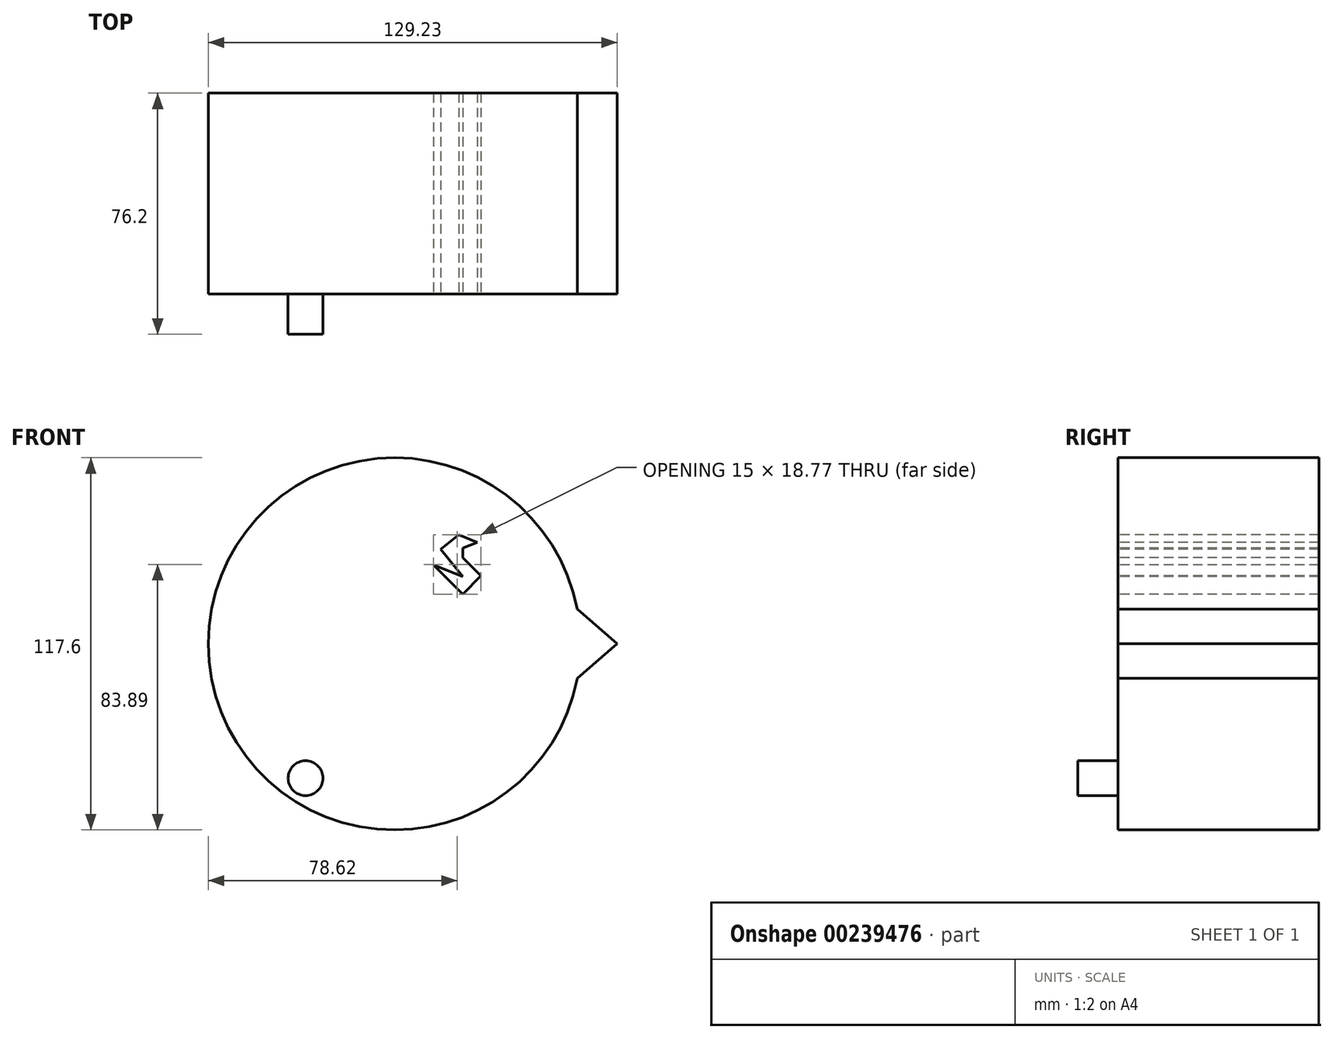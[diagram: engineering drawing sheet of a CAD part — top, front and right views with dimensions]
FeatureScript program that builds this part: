
annotation { "Feature Type Name" : "Feature", "Feature Type Description" : "" }
export const myFeature = defineFeature(function(context is Context, id is Id, definition is map)
    precondition{}
    {
        {
            var Q0;
            Q0=qCreatedBy(makeId("Front.planeOp"),FACE);
            var sketch = newSketch(context, id + "F0", { "sketchPlane" : qUnion([Q0])});
            skCircle(sketch, "E0", {"center": v(0, 0) * mm, "radius": 58.8 * mm});
            skSolve(sketch);
        }
        {
            var Q0;
            Q0=makeQuery(id+"F0.imprint","IMPRINT",FACE,{"disambiguationData":[TD([[makeQuery(id+"F0.imprint","IMPRINT",EDGE,{"derivedFrom":sQuery(id+"F0.wireOp",EDGE,"E0")}),1.0]])]});
            extrude(context, id + "F1", {"entities" : qUnion([Q0]), "endBound" : BoundingType.SYMMETRIC, "depth" : 63.5 * mm});
        }
        {
            var Q0;
            Q0=makeQuery(id+"F1.opExtrude","CAP_FACE",FACE,{"disambiguationData":[OSD([sQuery(id+"F0.wireOp",EDGE,"E0")])],"isStart":false});
            var sketch = newSketch(context, id + "F2", { "sketchPlane" : qUnion([Q0])});
            skCircle(sketch, "E1", {"center": v(-28.08, -42.43) * mm, "radius": 5.5 * mm});
            skSolve(sketch);
        }
        {
            var Q0;
            Q0=makeQuery(id+"F2.imprint","IMPRINT",FACE,{"disambiguationData":[TD([[makeQuery(id+"F2.imprint","IMPRINT",EDGE,{"derivedFrom":sQuery(id+"F2.wireOp",EDGE,"E1")}),1.0]])]});
            extrude(context, id + "F3", {"entities" : qUnion([Q0]), "operationType" : NewBodyOperationType.ADD, "depth" : 12.7 * mm});
        }
        {
            var Q0;
            Q0=makeQuery(id+"F1.opExtrude","CAP_FACE",FACE,{"disambiguationData":[OSD([sQuery(id+"F0.wireOp",EDGE,"E0")])],"isStart":false});
            var sketch = newSketch(context, id + "F4", { "sketchPlane" : qUnion([Q0])});
            skLineSegment(sketch, "E2", {"start": v(57.78, 10.93) * mm, "end": v(70.43, 0) * mm});
            skLineSegment(sketch, "E3", {"start": v(70.43, 0) * mm, "end": v(57.78, -10.93) * mm});
            skArc(sketch, "E4.0", {"start": v(57.78, -10.93) * mm, "mid": v(58.8, 0) * mm, "end": v(57.78, 10.93) * mm});
            skSolve(sketch);
        }
        {
            var Q0;
            Q0 = qSketchRegion(id + "F4", true);
            extrude(context, id + "F5", {"entities" : qUnion([Q0]), "operationType" : NewBodyOperationType.ADD, "oppositeDirection" : true, "depth" : 63.5 * mm});
        }
        {
            var Q0;
            {var subQ0=sQuery(id+"F4.wireOp",EDGE,"E4.0");var subQ1=sQuery(id+"F4.wireOp",EDGE,"E3");var subQ2=sQuery(id+"F4.wireOp",EDGE,"E2");Q0=makeQuery(id+"FHikPiwag3CsCLX_1.16.F5.boolean.opBoolean","MERGE",FACE,{"derivedFrom":[makeQuery(id+"FHikPiwag3CsCLX_1.15.F5.boolean.opBoolean","MERGE",FACE,{"derivedFrom":[makeQuery(id+"FHikPiwag3CsCLX_1.14.F5.boolean.opBoolean","MERGE",FACE,{"derivedFrom":[makeQuery(id+"FHikPiwag3CsCLX_1.13.F5.boolean.opBoolean","MERGE",FACE,{"derivedFrom":[makeQuery(id+"FHikPiwag3CsCLX_1.12.F5.boolean.opBoolean","MERGE",FACE,{"derivedFrom":[makeQuery(id+"FHikPiwag3CsCLX_1.11.F5.boolean.opBoolean","MERGE",FACE,{"derivedFrom":[makeQuery(id+"FHikPiwag3CsCLX_1.10.F5.boolean.opBoolean","MERGE",FACE,{"derivedFrom":[makeQuery(id+"FHikPiwag3CsCLX_1.9.F5.boolean.opBoolean","MERGE",FACE,{"derivedFrom":[makeQuery(id+"FHikPiwag3CsCLX_1.8.F5.boolean.opBoolean","MERGE",FACE,{"derivedFrom":[makeQuery(id+"FHikPiwag3CsCLX_1.7.F5.boolean.opBoolean","MERGE",FACE,{"derivedFrom":[makeQuery(id+"FHikPiwag3CsCLX_1.6.F5.boolean.opBoolean","MERGE",FACE,{"derivedFrom":[makeQuery(id+"FHikPiwag3CsCLX_1.5.F5.boolean.opBoolean","MERGE",FACE,{"derivedFrom":[makeQuery(id+"FHikPiwag3CsCLX_1.4.F5.boolean.opBoolean","MERGE",FACE,{"derivedFrom":[makeQuery(id+"FHikPiwag3CsCLX_1.3.F5.boolean.opBoolean","MERGE",FACE,{"derivedFrom":[makeQuery(id+"FHikPiwag3CsCLX_1.2.F5.boolean.opBoolean","MERGE",FACE,{"derivedFrom":[makeQuery(id+"FHikPiwag3CsCLX_1.1.F5.boolean.opBoolean","MERGE",FACE,{"derivedFrom":[makeQuery(id+"F5.boolean.opBoolean","MERGE",FACE,{"derivedFrom":[makeQuery(id+"F1.opExtrude","CAP_FACE",FACE,{"disambiguationData":[OSD([sQuery(id+"F0.wireOp",EDGE,"E0")])],"isStart":false}),makeQuery(id+"F5.opExtrude","CAP_FACE",FACE,{"disambiguationData":[OSD([subQ2,subQ1,subQ0])],"isStart":true})]}),makeQuery(id+"FHikPiwag3CsCLX_1.1.F5.opExtrude","CAP_FACE",FACE,{"disambiguationData":[OSD([subQ2,subQ1,subQ0])],"isStart":true})]}),makeQuery(id+"FHikPiwag3CsCLX_1.2.F5.opExtrude","CAP_FACE",FACE,{"disambiguationData":[OSD([subQ2,subQ1,subQ0])],"isStart":true})]}),makeQuery(id+"FHikPiwag3CsCLX_1.3.F5.opExtrude","CAP_FACE",FACE,{"disambiguationData":[OSD([subQ2,subQ1,subQ0])],"isStart":true})]}),makeQuery(id+"FHikPiwag3CsCLX_1.4.F5.opExtrude","CAP_FACE",FACE,{"disambiguationData":[OSD([subQ2,subQ1,subQ0])],"isStart":true})]}),makeQuery(id+"FHikPiwag3CsCLX_1.5.F5.opExtrude","CAP_FACE",FACE,{"disambiguationData":[OSD([subQ2,subQ1,subQ0])],"isStart":true})]}),makeQuery(id+"FHikPiwag3CsCLX_1.6.F5.opExtrude","CAP_FACE",FACE,{"disambiguationData":[OSD([subQ2,subQ1,subQ0])],"isStart":true})]}),makeQuery(id+"FHikPiwag3CsCLX_1.7.F5.opExtrude","CAP_FACE",FACE,{"disambiguationData":[OSD([subQ2,subQ1,subQ0])],"isStart":true})]}),makeQuery(id+"FHikPiwag3CsCLX_1.8.F5.opExtrude","CAP_FACE",FACE,{"disambiguationData":[OSD([subQ2,subQ1,subQ0])],"isStart":true})]}),makeQuery(id+"FHikPiwag3CsCLX_1.9.F5.opExtrude","CAP_FACE",FACE,{"disambiguationData":[OSD([subQ2,subQ1,subQ0])],"isStart":true})]}),makeQuery(id+"FHikPiwag3CsCLX_1.10.F5.opExtrude","CAP_FACE",FACE,{"disambiguationData":[OSD([subQ2,subQ1,subQ0])],"isStart":true})]}),makeQuery(id+"FHikPiwag3CsCLX_1.11.F5.opExtrude","CAP_FACE",FACE,{"disambiguationData":[OSD([subQ2,subQ1,subQ0])],"isStart":true})]}),makeQuery(id+"FHikPiwag3CsCLX_1.12.F5.opExtrude","CAP_FACE",FACE,{"disambiguationData":[OSD([subQ2,subQ1,subQ0])],"isStart":true})]}),makeQuery(id+"FHikPiwag3CsCLX_1.13.F5.opExtrude","CAP_FACE",FACE,{"disambiguationData":[OSD([subQ2,subQ1,subQ0])],"isStart":true})]}),makeQuery(id+"FHikPiwag3CsCLX_1.14.F5.opExtrude","CAP_FACE",FACE,{"disambiguationData":[OSD([subQ2,subQ1,subQ0])],"isStart":true})]}),makeQuery(id+"FHikPiwag3CsCLX_1.15.F5.opExtrude","CAP_FACE",FACE,{"disambiguationData":[OSD([subQ2,subQ1,subQ0])],"isStart":true})]}),makeQuery(id+"FHikPiwag3CsCLX_1.16.F5.opExtrude","CAP_FACE",FACE,{"disambiguationData":[OSD([subQ2,subQ1,subQ0])],"isStart":true})]});}
            var sketch = newSketch(context, id + "F6", { "sketchPlane" : qUnion([Q0])});
            skLineSegment(sketch, "E5", {"start": v(21.55, 27.24) * mm, "end": v(27.32, 21.47) * mm});
            skLineSegment(sketch, "E6", {"start": v(27.32, 21.47) * mm, "end": v(21.55, 15.7) * mm});
            skLineSegment(sketch, "E7", {"start": v(21.55, 15.7) * mm, "end": v(12.32, 24.94) * mm});
            skLineSegment(sketch, "E8", {"start": v(12.32, 24.94) * mm, "end": v(21.55, 21.28) * mm});
            skLineSegment(sketch, "E9", {"start": v(21.55, 21.28) * mm, "end": v(14.63, 29.94) * mm});
            skLineSegment(sketch, "E10", {"start": v(14.63, 29.94) * mm, "end": v(23.4, 36.95) * mm});
            skLineSegment(sketch, "E11", {"start": v(23.4, 36.95) * mm, "end": v(20.3, 34.48) * mm});
            skLineSegment(sketch, "E12", {"start": v(20.3, 34.48) * mm, "end": v(26.17, 32.05) * mm});
            skLineSegment(sketch, "E13", {"start": v(26.17, 32.05) * mm, "end": v(21.55, 30.32) * mm});
            skLineSegment(sketch, "E14", {"start": v(21.55, 30.32) * mm, "end": v(21.55, 27.24) * mm});
            skSolve(sketch);
        }
        {
            var Q0;
            Q0=makeQuery(id+"F6.imprint","IMPRINT",FACE,{"disambiguationData":[TD([[makeQuery(id+"F6.imprint","IMPRINT",EDGE,{"derivedFrom":sQuery(id+"F6.wireOp",EDGE,"E5")}),-1.0]])]});
            extrude(context, id + "F7", {"entities" : qUnion([Q0]), "operationType" : NewBodyOperationType.REMOVE, "oppositeDirection" : true, "depth" : 63.5 * mm});
        }
    });
